# Revit family: toledo_flat_round_e_901453_002_1_dd77
name_source: partatom
category: Lighting Fixtures
units: mm (PartAtom-declared; Revit-internal decimal feet)

## family parameters
Cut with Voids When Loaded = No
Host = Face
Light Source = No
Part Type = Normal
Room Calculation Point = No
Round Connector Dimension = Use Diameter
Shared = No

## types (1)
- TOLEDO FLAT round E (1 x LED Modul 840, 1800 lm, 4000)
    Apparent Load = 17 VA
    CIE Flux Codes = 48 79 96 100 100
    Color Rendering = 80
    Color Temperature = 4000
    Default Elevation = 1800 mm  [stored 5.90551 ft]
    Description = Series: TOLEDO FLAT round
Ultra thin recessed downlight. Housing: die-cast aluminium. Light guide and diffuser made of non-yellowing PMMA, opal matt. Ceiling installation with spring system. Mounting depth depends on ceiling strength. Including separate LED converter with connecting cable 250 mm. Suitable for through-wiring with separately available accessories. Surface mounted housing as accessory for all sizes. Retrofittable decorative cylinders made of chintz fabric as accessory, optional with satin finish plastic diffuser. Through-wiring box (5 pole) available as accessory. 
Colour: white
Diameter: 255 mm
Height: 3 mm
Cut-out diameter: 234 mm
Recess height: 30-56 mm
Luminaire: recess height: 31-51 mm
Lamp: LED
Socket: without socket
Colour temperature: 4000K
Colour rendering index (CRI): 80
System power: 17 W
Rated luminous flux: 1800 lm
Luminous efficiency: 106 lm/W
Control gear: Regulated power supply
Protection class: II
Type of protection: IP 54
    Height = 0 mm  [stored 0 ft]
    Lamp = 1 x LED Modul 840
    Lamp Light Flux = 1800 lm
    Lamp count = 1
    Length = 255 mm
    Lifetime = 50000 h
    Luminous efficacy = 106 lm/W
    Manufacturer = RZB
    ModVariant = No
    Model = 901453.002.1
    Mounting Place = Ceiling
    Mounting Type = Recessed
    Number of Poles = 1
    OnlyDefault = Yes
    Power Factor = 1
    Product Name = TOLEDO FLAT round E
    Product group = Recessed downlights
    ProductGroupID = 402
    Protection Class = Protection class II
    Protection Degree = IP 20
    RLX_Detail_Level = 1
    RLX_Emergency_Light_Flux = 0 lm
    RLX_Emergency_Type = 0
    RLX_Emergency_Type_DB = No
    RlxData = <blob elided: 77285 chars, md5=e50bb27d>
    Socket = socket
    Standby Power = 0 W
    System Light Flux = 1800 lm
    System Power = 17 W
    Type Comments = Product without accessories
    Type Image = 901453.002.jpg
    URL = http://relux.com
    VarID = ---
    Voltage = 230 V
    Voltage Range = 220-240 V
    Weight = 0.00 kg
    Width = 0 mm  [stored 0 ft]

note: [stored X ft] marks values corroborated as IEEE doubles in the binary element streams (Revit-internal decimal feet)

## geometry (parser evidence)
native form markers: Sweep x10
no freeform markers — native parametric forms only
